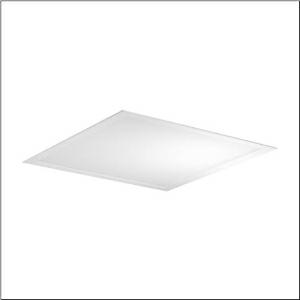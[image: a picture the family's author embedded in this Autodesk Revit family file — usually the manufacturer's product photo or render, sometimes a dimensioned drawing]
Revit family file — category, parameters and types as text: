
# Revit family: apollon_21_square_51mq11wd2m14
name_source: partatom
category: Lighting Fixtures
units: mm (PartAtom-declared; Revit-internal decimal feet)

## family parameters
Cut with Voids When Loaded = No
Host = Face
Light Source = No
Part Type = Normal
Room Calculation Point = No
Round Connector Dimension = Use Diameter
Shared = No

## types (1)
- --- (1 x LED, 4200 lm, 26 W, 4000K)
    Apparent Load = 26 VA
    CIE Flux Codes = 60 87 97 100 100
    Color Rendering = 80
    Color Temperature = 4000K
    Default Elevation = 1800 mm
    Description = Apollon 21 square, office luminaire, primary optical cover: micro prismatic cover, of PMMA, CAT 2 (L<= 3000cd/m²), light emission: direct distribution, primary light characteristic: symmetric, installation type: lay-in mounting, LED, rated luminous flux: 4.200lm, luminous efficacy: 162lm/W, light colour: 830/840, colour temperature: 3000/4000K, control gear: DALI 2, Multilumen, with terminal, 5-pole, mains connection: 220..240V, AC/DC, 0/50..60Hz, rated input power: 26W, housing, of aluminium, coated, traffic white (RAL 9016), module: M625, length: 620mm, width: 620mm, height: 55mm, recess depth: 180mm, housing upper side, of sheet steel, galvanised, protection rating (complete): IP20, protection rating (lamp compartment, on room side): IP50, insulation class (complete): insulation class II (safety insulation), certification: CE, ENEC, impact resistance: IK03, permissible operating ambient temperature: -20..+45°C, permissible storage temperature: -40..+80°C, standard: EN 60598-2-22, packaging unit: 1 piece
    Height = 0 mm  [stored 0 ft]
    Lamp = 1 x LED
    Lamp Light Flux = 4200 lm
    Lamp Power = 26 W
    Lamp count = 1
    Length = 620 mm
    Luminous efficacy = 162 lm/W
    Manufacturer = Siteco
    ModVariant = No
    Model = 51MQ11WD2M14
    Mounting Place = Ceiling
    Mounting Type = Recessed
    Number of Poles = 1
    OnlyDefault = Yes
    Power Factor = 1
    Product Name = Apollon 21 square
    Product group = office luminaire | ceiling recessed
    ProductGroupID = 401
    Protection Class = Protection class II
    Protection Degree = IP 20
    RLX_Detail_Level = 1
    RLX_Emergency_Light_Flux = 0 lm
    RLX_Emergency_Type = 0
    RLX_Emergency_Type_DB = No
    RlxData = <blob elided: 13217 chars, md5=252c13ec>
    Socket = socket
    Standby Power = 0 W
    System Light Flux = 4200 lm
    System Power = 26 W
    Type Comments = factory setting
    Type Image = l_1291054.jpg
    URL = http://relux.com
    VarID = @adj_068454
    Voltage = 0 V
    Weight = 0.00 kg
    Width = 620 mm

note: [stored X ft] marks values corroborated as IEEE doubles in the binary element streams (Revit-internal decimal feet)

## geometry (parser evidence)
native form markers: Sweep x11
no freeform markers — native parametric forms only
